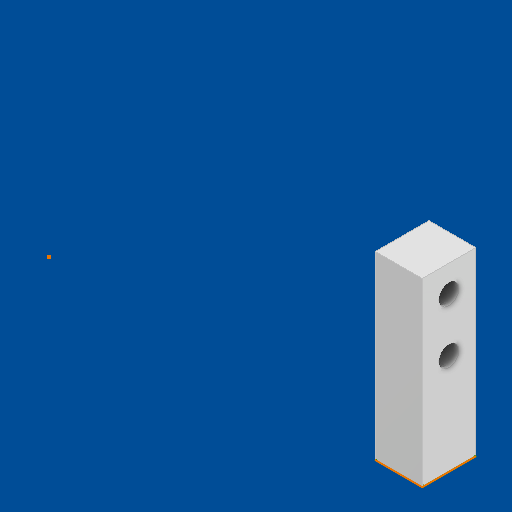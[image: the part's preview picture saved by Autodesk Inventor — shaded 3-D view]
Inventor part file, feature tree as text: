
AUTODESK INVENTOR PART (.ipt)
format: ipt  version: 2025 (Build 290162000, 162)  size: 181,248 bytes
history: native  units: in
note: dims shown in document units (in); Inventor stores cm internally (conversion verified against a paired STEP export)
features: direct_edit x6, other x6, move_body x5, hole x2, sketch x2, plane x1, split x1
ambient origin geometry x8: Origin, YZ Plane, XZ Plane, XY Plane, X Axis, Y Axis, Z Axis, Center Point
bodies: Solid1 (feature_tree), Body3 (feature_tree)
feature tree (23):
  move_body  "Move Body1"
  direct_edit  "Direct Edit1"
  direct_edit  "Direct Edit2"
  direct_edit  "Direct Edit3"
  hole  "Hole1"  [1 undecoded]
  direct_edit  "Direct Edit4"
  plane  "Work Plane1"
  split  "Split1"
  direct_edit  "Direct Edit5"
  sketch  "Sketch3"  dims[d2=0.0625in d3=0.0625in d4=0.1181in d5=0.0in d6=0.0089in d7=90.0deg d8=0.0968in d9=0.2362in d10=0.1575in d11=0.0787in d12=90.0deg d13=0.3465in d14=0.8108in d15=0.0039in d16=0.0039in d17=-0.315in d19=0.0in d20=0.0in d21=0.4154in d42=0.3937in d43=0.3937in d32=0.1936in d33=0.3543in d34=0.1575in d35=0.0787in d36=90.0deg d37=0.3543in d38=0.8108in d47=0.0102in d48=0.0in d49=0.0in d50=0.0in d51=-0.0043in d52=0.0in d53=0.0in d54=-0.0043in d55=0.0in d22=0.0197in d23=0.0344in d24=0.0197in d25=0.0344in]
  other  "Work Point1"
  hole  "Hole3"  [1 undecoded]
  direct_edit  "Direct Edit8"
  sketch  "Sketch1"  dims[d0=45.0deg d1=0.0059in]
  other  "Size1"
  other  "Size2"
  other  "Size3"
  other  "Size4"
  other  "Size5"
  move_body  "Move1"
  move_body  "Move4"
  move_body  "Move5"
  move_body  "Move6"
note: 2 required parameter values undecoded (feature->parameter linkage not recoverable at this tier; creation-order binding heuristic only, values carry confidence <= 0.55)
